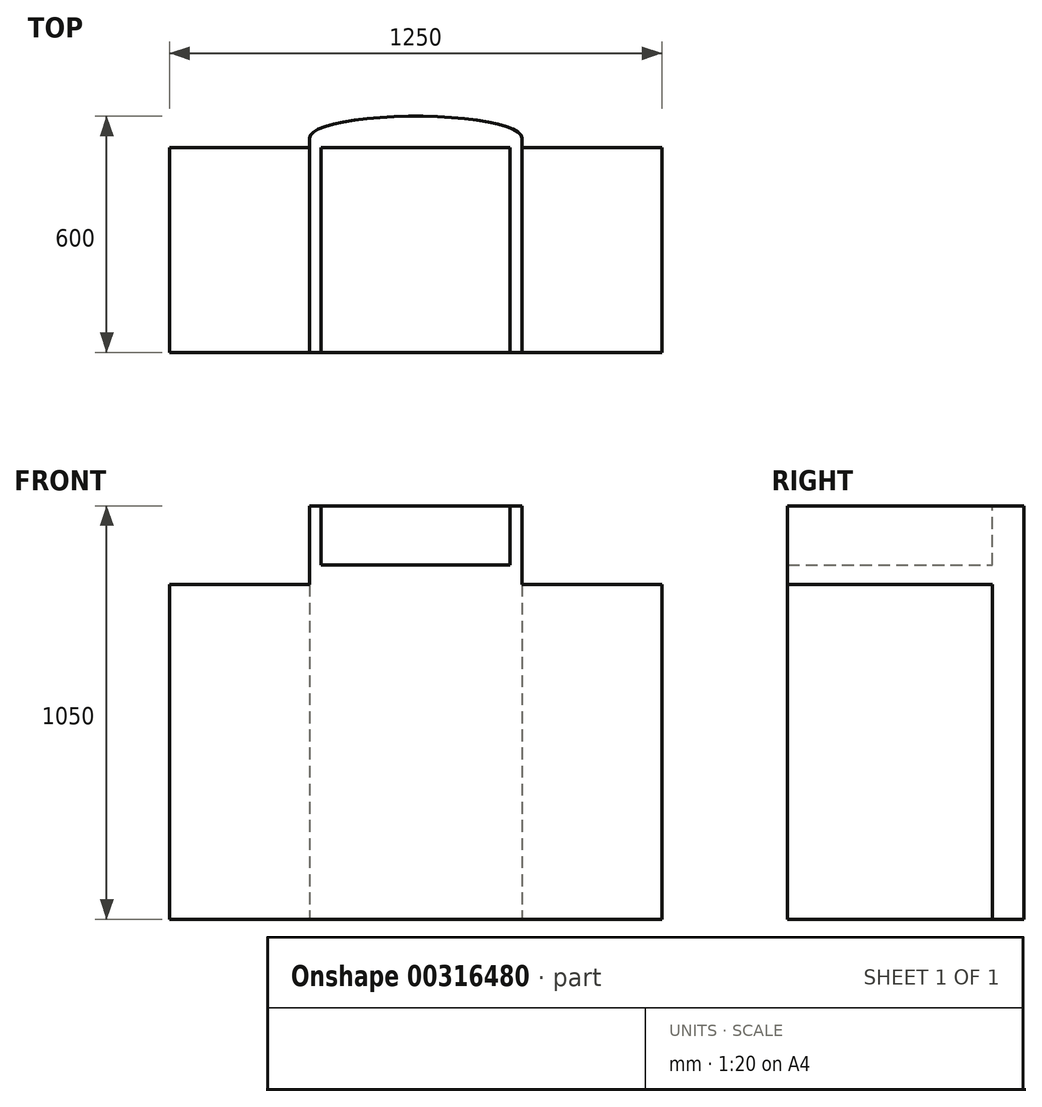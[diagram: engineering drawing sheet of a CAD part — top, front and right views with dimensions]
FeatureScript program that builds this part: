
annotation { "Feature Type Name" : "Feature", "Feature Type Description" : "" }
export const myFeature = defineFeature(function(context is Context, id is Id, definition is map)
    precondition{}
    {
        {
            var Q0;
            Q0=qCreatedBy(makeId("Top.planeOp"),FACE);
            var sketch = newSketch(context, id + "F0", { "sketchPlane" : qUnion([Q0])});
            skLineSegment(sketch, "E0", {"start": v(0, 0) * mm, "end": v(1250, 0) * mm});
            skLineSegment(sketch, "E1", {"start": v(1250, 0) * mm, "end": v(1250, 520) * mm});
            skLineSegment(sketch, "E2", {"start": v(1250, 520) * mm, "end": v(895, 520) * mm});
            skLineSegment(sketch, "E3", {"start": v(895, 520) * mm, "end": v(895, 545) * mm});
            skLineSegment(sketch, "E4", {"start": v(355, 545) * mm, "end": v(355, 520) * mm});
            skLineSegment(sketch, "E5", {"start": v(355, 520) * mm, "end": v(0, 520) * mm});
            skLineSegment(sketch, "E6", {"start": v(0, 520) * mm, "end": v(0, 0) * mm});
            skEllipticalArc(sketch, "E7", {});
            const initialGuessF0  = {"E7": [0.625, 0.545, -1, 0, 0.27, 0.055, 3.1415926535897927, 6.283185307179585]};
            skSetInitialGuess(sketch, initialGuessF0);
            skSolve(sketch);
        }
        {
            var Q0;
            Q0=makeQuery(id+"F0.imprint","IMPRINT",FACE,{"disambiguationData":[TD([[makeQuery(id+"F0.imprint","IMPRINT",EDGE,{"derivedFrom":sQuery(id+"F0.wireOp",EDGE,"E0")}),1.0]])]});
            extrude(context, id + "F1", {"entities" : qUnion([Q0]), "depth" : 850 * mm});
        }
        {
            var Q0;
            Q0=makeQuery(id+"F1.opExtrude","CAP_FACE",FACE,{"disambiguationData":[OSD([sQuery(id+"F0.wireOp",EDGE,"E0"),sQuery(id+"F0.wireOp",EDGE,"E1"),sQuery(id+"F0.wireOp",EDGE,"E2"),sQuery(id+"F0.wireOp",EDGE,"E3"),sQuery(id+"F0.wireOp",EDGE,"E4"),sQuery(id+"F0.wireOp",EDGE,"E5"),sQuery(id+"F0.wireOp",EDGE,"E6"),sQuery(id+"F0.wireOp",EDGE,"E7")])],"isStart":false});
            var sketch = newSketch(context, id + "F2", { "sketchPlane" : qUnion([Q0])});
            skEllipticalArc(sketch, "E8.0", {});
            skLineSegment(sketch, "E9.0", {"start": v(355, 0) * mm, "end": v(895, 0) * mm});
            skLineSegment(sketch, "E10.0", {"start": v(355, 545) * mm, "end": v(355, 0) * mm});
            skLineSegment(sketch, "E11.0", {"start": v(895, 0) * mm, "end": v(895, 545) * mm});
            skPoint(sketch, "E12.orphan", {"position": v(895, 520) * mm});
            skPoint(sketch, "E13.orphan", {"position": v(355, 520) * mm});
            skPoint(sketch, "E14.orphan", {"position": v(1250, 0) * mm});
            skPoint(sketch, "E15.orphan", {"position": v(0, 0) * mm});
            const initialGuessF2  = {"E8.0": [0.625, 0.545, -1, 0, 0.27, 0.055, 3.1415926535897927, 6.283185307179585]};
            skSetInitialGuess(sketch, initialGuessF2);
            skSolve(sketch);
        }
        {
            var Q0;
            {var subQ4=sQuery(id+"F2.wireOp",EDGE,"E8.0");Q0=makeQuery(id+"F2.imprint","IMPRINT",FACE,{"disambiguationData":[TD([[makeQuery(id+"F2.imprint","IMPRINT",EDGE,{"derivedFrom":subQ4}),1.0]])]});}
            extrude(context, id + "F3", {"entities" : qUnion([Q0]), "operationType" : NewBodyOperationType.ADD, "depth" : 200 * mm});
        }
        {
            var Q0;
            Q0=makeQuery(id+"F3.opExtrude","CAP_FACE",FACE,{"disambiguationData":[OSD([sQuery(id+"F2.wireOp",EDGE,"E8.0"),sQuery(id+"F2.wireOp",EDGE,"E9.0"),sQuery(id+"F2.wireOp",EDGE,"E10.0"),sQuery(id+"F2.wireOp",EDGE,"E11.0")])],"isStart":false});
            var sketch = newSketch(context, id + "F4", { "sketchPlane" : qUnion([Q0])});
            skLineSegment(sketch, "E16.bottom", {"start": v(385, 0) * mm, "end": v(865, 0) * mm});
            skLineSegment(sketch, "E16.top", {"start": v(385, 520) * mm, "end": v(865, 520) * mm});
            skLineSegment(sketch, "E16.left", {"start": v(385, 0) * mm, "end": v(385, 520) * mm});
            skLineSegment(sketch, "E16.right", {"start": v(865, 0) * mm, "end": v(865, 520) * mm});
            skSolve(sketch);
        }
        {
            var Q0;
            Q0=makeQuery(id+"F4.imprint","IMPRINT",FACE,{"disambiguationData":[TD([[makeQuery(id+"F4.imprint","IMPRINT",EDGE,{"derivedFrom":sQuery(id+"F4.wireOp",EDGE,"E16.bottom")}),1.0]])]});
            extrude(context, id + "F5", {"entities" : qUnion([Q0]), "operationType" : NewBodyOperationType.REMOVE, "oppositeDirection" : true, "depth" : 150 * mm});
        }
    });
